# Revit family: Kabelrinne MKSM- MKSM 615 FS_ok
name_source: partatom
category: Generic Models
revit_build: Autodesk Revit 2017 (Build: 20190508_0315(x64)
units: mm (PartAtom-declared; Revit-internal decimal feet)

## family parameters
Always vertical = Yes
Can host rebar = No
Cut with Voids When Loaded = No
Part Type = Normal
Room Calculation Point = No
Round Connector Dimension = Use Diameter
Shared = No
Work Plane-Based = No

## types (6) — shared parameters
Cut's number = 2
Length = 3050 mm  [stored 10.0066 ft]
Length 1 = 3000 mm  [stored 9.84252 ft]
Length 2 = 50 mm  [stored 0.164042 ft]
Manufacturer = OBO BETTERMANN
Material = Strip-galvanised
URL = http://www.obo-bettermann.com
Width 2 = 7 mm  [stored 0.0229659 ft]

## per-type parameters (varying)
| type | GTIN | Manufacturer Art.No. | Width | Width 1 |
| MKSM 630 FS | 4012195829959 | 6059006 | 300 mm | 150 mm  [stored 0.492126 ft] |
| MKSM 640 FS | 4012195829966 | 6059008 | 400 mm  [stored 1.31234 ft] | 200 mm  [stored 0.656168 ft] |
| MKSM 650 FS | 4012195829973 | 6059010 | 500 mm  [stored 1.64042 ft] | 250 mm  [stored 0.82021 ft] |
| MKSM 660 FS | 4012195829980 | 6059012 | 600 mm | 300 mm |
| MKSM 615 FS | 4012195829935 | 6059002 | 150 mm  [stored 0.492126 ft] | 75 mm |
| MKSM 620 FS | 4012195829942 | 6059004 | 200 mm  [stored 0.656168 ft] | 100 mm  [stored 0.328084 ft] |

note: column(s) folded — value = type name in every type: Article Type

note: [stored X ft] marks values corroborated as IEEE doubles in the binary element streams (Revit-internal decimal feet)

## geometry (parser evidence)
native form markers: Sweep x2
no freeform markers — native parametric forms only
